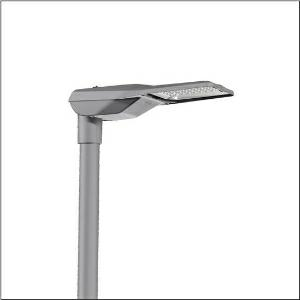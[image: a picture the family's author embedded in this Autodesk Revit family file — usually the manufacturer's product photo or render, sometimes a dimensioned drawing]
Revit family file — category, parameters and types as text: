
# Revit family: streetlight_sl_21_iq_mini___p0_8ab_5xe2r31v08jb_ae49
name_source: partatom
category: Lighting Fixtures
units: mm (PartAtom-declared; Revit-internal decimal feet)

## family parameters
Cut with Voids When Loaded = No
Host = Face
Light Source = No
Part Type = Normal
Room Calculation Point = No
Round Connector Dimension = Use Diameter
Shared = No

## types (1)
- --- (1 x LED, 9740 lm, 72.5 W, 3000K)
    Apparent Load = 73 VA
    CIE Flux Codes = 39 72 97 100 100
    Color Rendering = 70
    Color Temperature = 3000K
    Default Elevation = 1800 mm
    Description = Streetlight SL 21 iQ mini, mast luminaire, primary light control with lens, of PMMA, primary optical cover: cover, of toughened safety glass, transparent, light distribution: P0.8aB, light emission: direct distribution, primary light characteristic: asymmetric, installation type: post-top, side-entry, LED, High Power LED, rated luminous flux: 9.740lm, luminous efficacy: 134lm/W, light colour: 730, colour temperature: 3000K, control gear: iQ-Street Remote, D4i with power reduction, control: pre-setting: logarithmic dimming characteristic, Street-Remote, Auto-Match, Temp-Guard, Lumen-Switch, Night-Set, Smart-Wire, Light-Fading, Desk-Remote (wireless, voltage-free reading and setting of iQ features in the workshop via application-optimized NFC function/RFID function), optimised constant luminous flux control (CLO 2.0), mains connection: 220..240V, AC, 50/60Hz, start of lifetime: 73W, end of service life: 76W, reduction: 33W, luminaire housing, of diecast aluminium, powder-coated, SITECO metallic grey (DB 702S), corrosivity category C5 high according to DIN EN ISO 12944, please order mast flange separately, inclination adjustable: 0°, 5°, 10°, 15°, sealing non-destructively replaceable, multi-level sealing system, length: 628mm, width: 235mm, height: 110mm, mast flange for spigot size: 42mm (side-entry): 5XC10008XM4, 60/48mm (side-entry/post-top): 5XC10108XM2, 76/60mm (side-entry/post-top): 5XC10108XM1, mounting height: 4..8m, Smart Interface above, protection rating (complete): IP66, insulation class (complete): insulation class II (safety insulation), certification: CE, ENEC, ENEC+, VDE, impact resistance: IK10, permissible operating ambient temperature for outdoor applications: -40..+50°C, standard-compliant lighting for roads and squares, packaging unit: 1 piece

Light Distribution: P0.8aB
    Height = 110 mm
    Lamp = 1 x LED
    Lamp Light Flux = 9740 lm
    Lamp Power = 72.5 W
    Lamp count = 1
    Length = 625 mm
    Luminous efficacy = 134 lm/W
    Manufacturer = Siteco
    ModVariant = No
    Model = 5XE2R31V08JB
    Number of Poles = 1
    OnlyDefault = Yes
    Power Factor = 1
    Product Name = Streetlight SL 21 iQ mini | P0.8aB
    Product group = mast luminaire | pylon top
    ProductGroupID = 6100
    Protection Class = Protection class II
    Protection Degree = IP 66
    RLX_Detail_Level = 1
    RLX_Emergency_Light_Flux = 0 lm
    RLX_Emergency_Type = 0
    RLX_Emergency_Type_DB = No
    RlxData = <blob elided: 92273 chars, md5=68b53161>
    Socket = socket
    Standby Power = 0 W
    System Light Flux = 9740 lm
    System Power = 73 W
    Type Comments = factory setting: luminous flux: 100 % | dim-lin: 254 | 755 mA
    Type Image = l_1003515.jpg
    URL = http://relux.com
    VarID = @adj_079067
    Voltage = 0 V
    Weight = 0.00 kg
    Width = 234 mm

## geometry (parser evidence)
native form markers: Blend x4, Sweep x11
no freeform markers — native parametric forms only
